# Revit family: Security_DoorStation_AiPhone_DVF-Surface
name_source: partatom
category: Generic Models
units: mm (PartAtom-declared; Revit-internal decimal feet)

## family parameters
Always vertical = No
Can host rebar = No
Cut with Voids When Loaded = No
Maintain Annotation Orientation = No
Part Type = Normal
Room Calculation Point = No
Round Connector Dimension = Use Diameter
Shared = No
Work Plane-Based = Yes

## types (1)
- Security_DoorStation_AiPhone_DVF-Surface
    Assembly Code = E1010100
    Construction Details = http://www.arcat.com
    Default Elevation = 4'-0"
    Description = Security and Communications Device as Specified in 28 16 00
    Expected Lifespan (Years) = 0
    HID Reader = Yes
    Installation-Fabrication = http://www.aiphone.com
    Keynote = 28 16 00
    Maintenance Schedule (Months) = 0
    Manufacturer = Aiphone Corp.
    Manufacturer Fax = 425-455-0071
    Manufacturer Website = http://www.aiphone.com
    Material = Metal - Aluminum - AiPhone - Cast
    Model = As Specified in 28 16 00
    Product Data = http://www.arcat.com
    Product Properties = http://www.arcat.com
    Proximity Card Reader = No
    Reader = Yes
    Reader Material = Plastic - AiPhone - Gray
    Revision = R1_10-2010
    Sales Information = http://www.aiphone.com
    Send Message = http://www.arcat.com
    Specification = http://www.arcat.com
    URL = http://www.aiphone.com
    Unit Depth = 1 3/4"
    Unit Height = 11 5/8"
    Unit Width = 5 3/4"
    Warranty Duration (Years) = 0

## geometry (parser evidence)
native form markers: Sweep x4
no freeform markers — native parametric forms only
